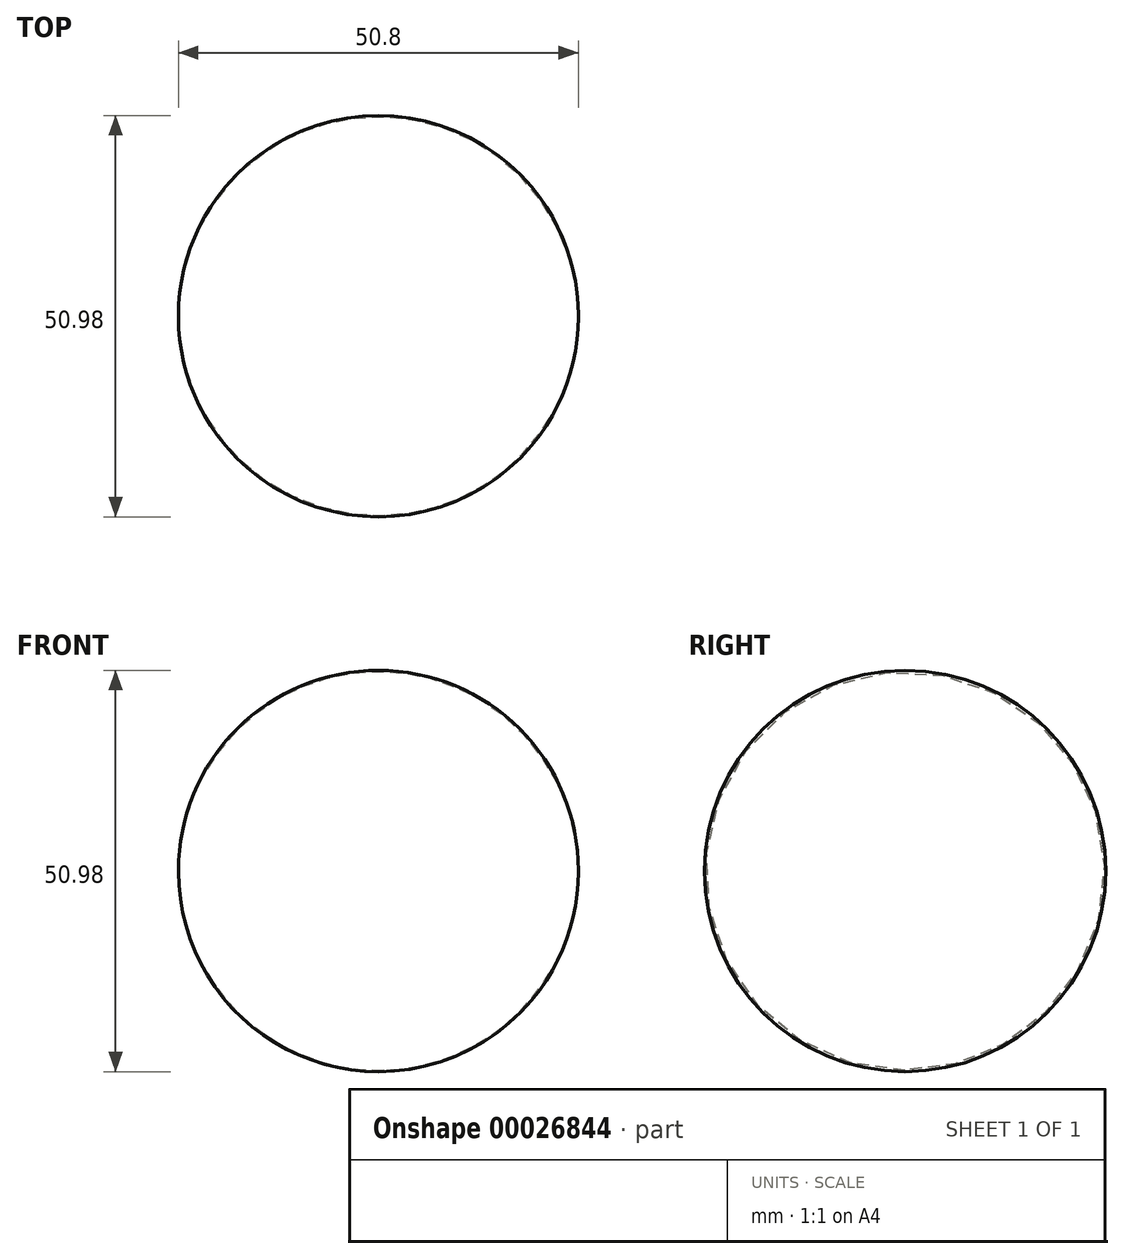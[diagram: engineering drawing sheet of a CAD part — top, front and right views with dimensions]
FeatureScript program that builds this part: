
annotation { "Feature Type Name" : "Feature", "Feature Type Description" : "" }
export const myFeature = defineFeature(function(context is Context, id is Id, definition is map)
    precondition{}
    {
        {
            var Q0;
            Q0=qCreatedBy(makeId("Front.planeOp"),FACE);
            var sketch = newSketch(context, id + "F0", { "sketchPlane" : qUnion([Q0])});
            skLineSegment(sketch, "E0", {"start": v(-19.31, 0) * mm, "end": v(31.49, 0) * mm});
            skArc(sketch, "E1", {"start": v(31.49, 0) * mm, "mid": v(6.09, 25.49) * mm, "end": v(-19.31, 0) * mm});
            skSolve(sketch);
        }
        {
            var Q0;
            Q0=makeQuery(id+"F0.imprint","IMPRINT",FACE,{"disambiguationData":[TD([[makeQuery(id+"F0.imprint","IMPRINT",EDGE,{"derivedFrom":sQuery(id+"F0.wireOp",EDGE,"E0")}),1.0]])]});
            var Q1;
            Q1=sQuery(id+"F0.wireOp",EDGE,"E0");
            revolve(context, id + "F1", {"entities" : qUnion([Q0]), "axis" : qUnion([Q1]), "revolveType" : RevolveType.FULL});
        }
    });
